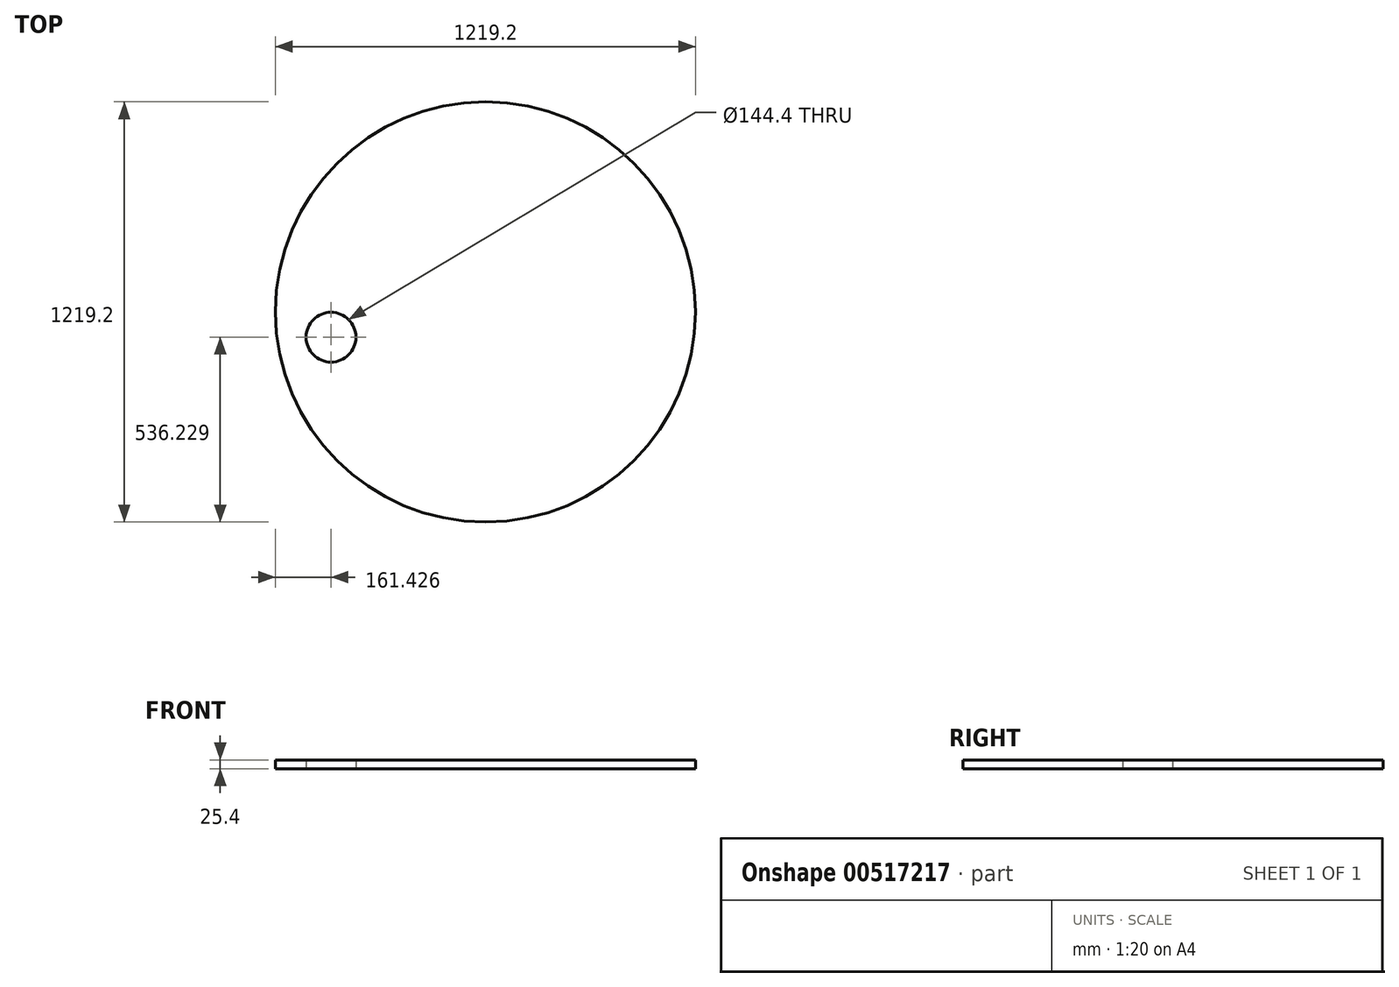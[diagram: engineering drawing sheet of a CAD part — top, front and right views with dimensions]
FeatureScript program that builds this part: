
annotation { "Feature Type Name" : "Feature", "Feature Type Description" : "" }
export const myFeature = defineFeature(function(context is Context, id is Id, definition is map)
    precondition{}
    {
        {
            var Q0;
            Q0=qCreatedBy(makeId("Top.planeOp"),FACE);
            var sketch = newSketch(context, id + "F0", { "sketchPlane" : qUnion([Q0])});
            skCircle(sketch, "E0", {"center": v(0, 0) * mm, "radius": 609.6 * mm});
            skSolve(sketch);
        }
        {
            var Q0;
            Q0=makeQuery(id+"F0.imprint","IMPRINT",FACE,{"disambiguationData":[TD([[makeQuery(id+"F0.imprint","IMPRINT",EDGE,{"derivedFrom":sQuery(id+"F0.wireOp",EDGE,"E0")}),1.0]])]});
            extrude(context, id + "F1", {"entities" : qUnion([Q0]), "depth" : 25.4 * mm, "offsetDistance" : 25.4 * mm});
        }
        {
            var Q0;
            Q0=qCreatedBy(makeId("Top.planeOp"),FACE);
            var sketch = newSketch(context, id + "F2", { "sketchPlane" : qUnion([Q0])});
            skCircle(sketch, "E1", {"center": v(-448.17, -73.37) * mm, "radius": 72.2 * mm});
            skSolve(sketch);
        }
        {
            var Q0;
            Q0 = qSketchRegion(id + "F2", true);
            extrude(context, id + "F3", {"entities" : qUnion([Q0]), "operationType" : NewBodyOperationType.REMOVE, "endBound" : BoundingType.THROUGH_ALL, "depth" : 25.4 * mm, "offsetDistance" : 25.4 * mm});
        }
    });
